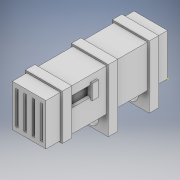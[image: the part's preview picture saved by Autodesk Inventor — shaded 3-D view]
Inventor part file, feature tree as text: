
AUTODESK INVENTOR PART (.ipt)
format: ipt  version: 2021 (Build 250183000, 183)  size: 350,720 bytes
history: native  units: mm
features: sketch x15, extrude x12, plane x1
ambient origin geometry x8: Origin, YZ Plane, XZ Plane, XY Plane, X Axis, Y Axis, Z Axis, Center Point
bodies: Solid1 (feature_tree)
feature tree (28):
  extrude  "Extrusion1"  Depth=50.8mm
  extrude  "Extrusion2"  Depth=3.742mm
  sketch  "Sketch3"  dims[d5=50.292mm d6=5.021mm]
  plane  "Work Plane1"
  extrude  "Extrusion3"  Depth=5.021mm
  sketch  "Sketch4"  dims[d7=6.604mm d8=8.704mm]
  extrude  "Extrusion4"  Depth=8.704mm
  extrude  "Extrusion5"  Depth=3.742mm
  extrude  "Extrusion6"  Depth=8.704mm
  sketch  "Sketch8"  dims[d17=184.0mm d18=0.0mm d19=94.707mm]
  extrude  "Extrusion7"  Depth=8.704mm
  sketch  "Sketch10"  dims[d22=2.54mm d23=94.707mm d24=14.463mm]
  sketch  "Sketch11"  dims[d25=68.58mm d26=14.463mm d27=2.54mm d28=2.54mm]
  extrude  "Extrusion8"  Depth=94.707mm
  extrude  "Extrusion9"  Depth=15.895mm
  extrude  "Extrusion10"  Depth=94.707mm
  sketch  "Sketch13"  dims[d31=2.54mm]
  extrude  "Extrusion11"  Depth=2.54mm
  extrude  "Extrusion12"  Depth=55.369mm
  sketch  "Sketch1"  dims[d0=63.5mm d1=50.8mm]
  sketch  "Sketch2"  dims[d2=184.15mm d3=0.0mm d4=3.742mm]
  sketch  "Sketch5"  dims[d9=6.604mm d10=3.742mm]
  sketch  "Sketch6"  dims[d11=3.742mm d12=8.704mm]
  sketch  "Sketch7"  dims[d13=3.742mm d16=8.704mm]
  sketch  "Sketch9"  dims[d20=14.463mm d21=15.895mm]
  sketch  "Sketch12"  dims[d29=47.547mm d30=55.369mm]
  sketch  "Sketch14"  dims[d32=55.88mm d33=0.0mm]
  sketch  "Sketch15"  dims[d34=6.982mm d35=85.239mm d36=3.725mm d37=6.982mm d38=85.239mm d39=3.725mm d40=4.53mm d41=4.53mm d42=61.42mm d43=5.881mm d44=3.287mm d45=2.54mm d46=0.0mm d48=9.417mm d49=14.937mm d50=9.819mm d51=22.975mm d52=1.905mm d53=0.0mm d54=13.021mm d55=16.131mm d56=6.926mm d57=0.0mm d58=16.131mm d59=1.905mm d60=9.417mm d61=0.0mm d62=27.142mm d63=14.282mm d64=24.181mm d65=24.181mm d66=14.282mm d67=27.142mm d68=30.0mm d69=0.0mm d70=30.0mm d71=0.0mm d72=0.127mm d73=0.684mm d74=24.765mm d75=500.0mm d76=0.0mm d77=31.015mm d80=9.819mm d81=9.417mm d82=22.975mm d83=5.021mm d84=0.0mm d85=16.131mm d86=13.021mm d87=5.021mm d88=0.0mm d78=0.872665mm]
